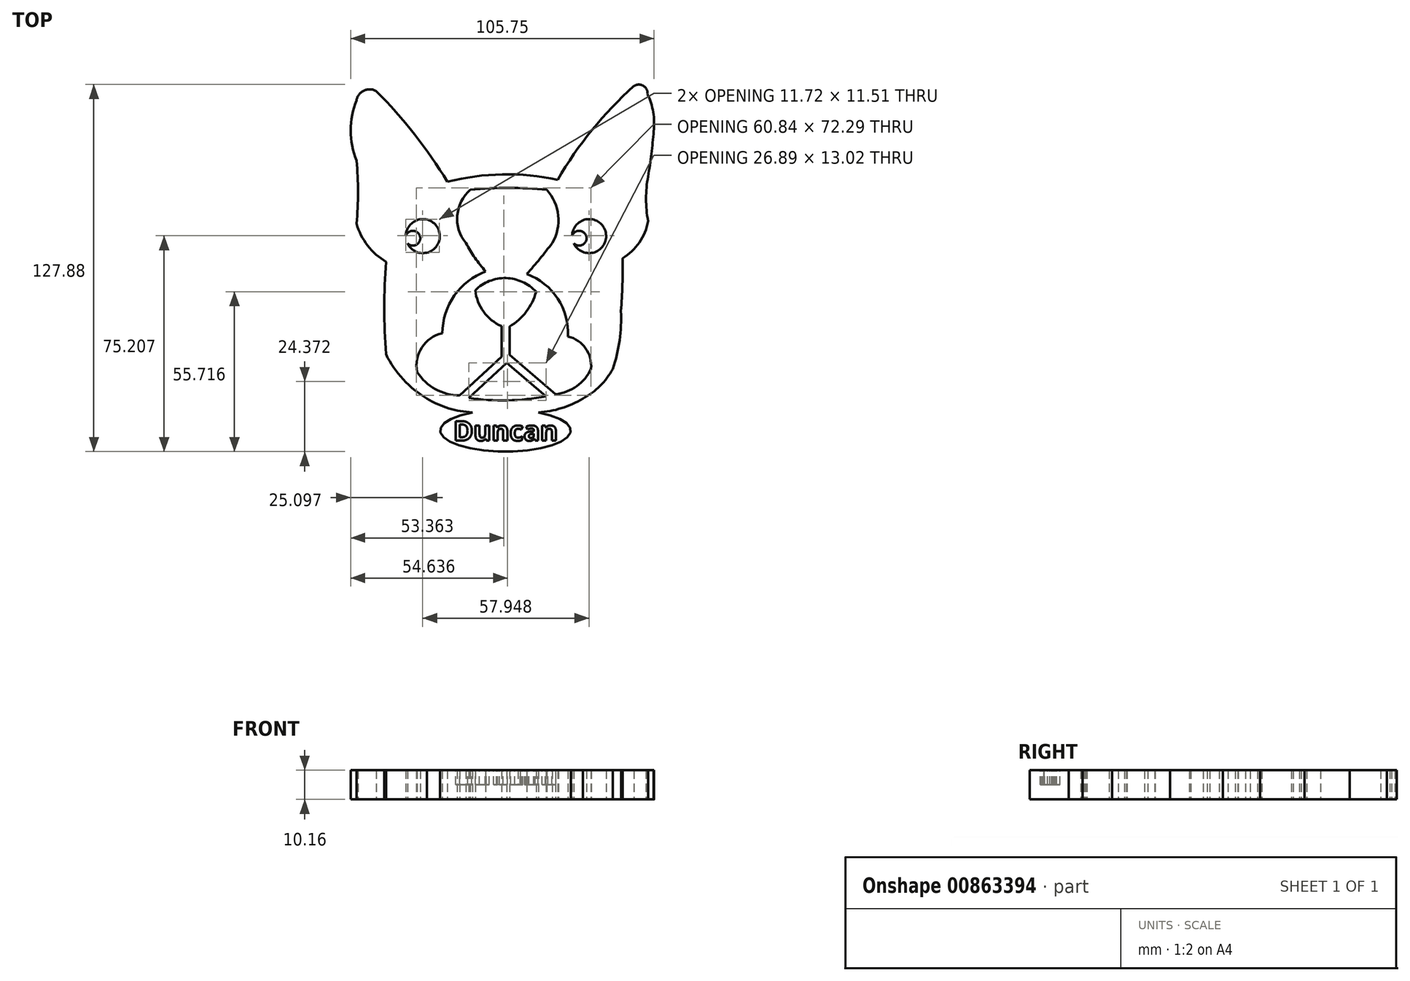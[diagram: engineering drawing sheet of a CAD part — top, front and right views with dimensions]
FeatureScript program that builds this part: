
annotation { "Feature Type Name" : "Feature", "Feature Type Description" : "" }
export const myFeature = defineFeature(function(context is Context, id is Id, definition is map)
    precondition{}
    {
        {
            var Q0;
            Q0=qCreatedBy(makeId("Top.planeOp"),FACE);
            var sketch = newSketch(context, id + "F0", { "sketchPlane" : qUnion([Q0])});
            skPoint(sketch, "E0", {"position": v(0, 0) * mm});
            skArc(sketch, "E1", {"start": v(19.56, 24.33) * mm, "mid": v(0.31, 26.2) * mm, "end": v(-18.85, 23.63) * mm});
            skArc(sketch, "E2", {"start": v(-18.85, 23.63) * mm, "mid": v(-30.3, 40.16) * mm, "end": v(-43.63, 55.21) * mm});
            skArc(sketch, "E3", {"start": v(-50.53, 9.03) * mm, "mid": v(-46.65, 1.42) * mm, "end": v(-40.27, -4.25) * mm});
            skArc(sketch, "E4", {"start": v(-50.53, 9.03) * mm, "mid": v(-50, 20) * mm, "end": v(-50.53, 30.98) * mm});
            skArc(sketch, "E5", {"start": v(-50.53, 52.04) * mm, "mid": v(-52.59, 41.5) * mm, "end": v(-50.53, 30.98) * mm});
            skArc(sketch, "E6", {"start": v(-43.63, 55.21) * mm, "mid": v(-47.9, 55.41) * mm, "end": v(-50.53, 52.04) * mm});
            skArc(sketch, "E7", {"start": v(46.1, 57) * mm, "mid": v(31.57, 41.69) * mm, "end": v(19.56, 24.33) * mm});
            skArc(sketch, "E8", {"start": v(42.14, -3) * mm, "mid": v(48.03, 2.47) * mm, "end": v(51.07, 9.91) * mm});
            skArc(sketch, "E9", {"start": v(51.07, 25.49) * mm, "mid": v(50.36, 17.7) * mm, "end": v(51.07, 9.91) * mm});
            skArc(sketch, "E10", {"start": v(51.07, 25.49) * mm, "mid": v(52.23, 33.34) * mm, "end": v(53.01, 41.24) * mm});
            skArc(sketch, "E11", {"start": v(50.89, 54.16) * mm, "mid": v(49.39, 57.08) * mm, "end": v(46.1, 57) * mm});
            skArc(sketch, "E12", {"start": v(53.01, 41.24) * mm, "mid": v(52.85, 47.85) * mm, "end": v(50.89, 54.16) * mm});
            skArc(sketch, "E13", {"start": v(-40.27, -4.25) * mm, "mid": v(-40.85, -20.36) * mm, "end": v(-40.27, -36.46) * mm});
            skArc(sketch, "E14", {"start": v(-40.27, -36.46) * mm, "mid": v(-34.27, -45.21) * mm, "end": v(-26.01, -51.87) * mm});
            skArc(sketch, "E15", {"start": v(-26.01, -51.87) * mm, "mid": v(-17.36, -55.6) * mm, "end": v(-8, -56.73) * mm});
            skArc(sketch, "E16", {"start": v(-8, -56.73) * mm, "mid": v(2.03, -57.3) * mm, "end": v(12.06, -56.73) * mm});
            skArc(sketch, "E17", {"start": v(12.06, -56.73) * mm, "mid": v(20.5, -55.35) * mm, "end": v(28.33, -51.87) * mm});
            skArc(sketch, "E18", {"start": v(28.33, -51.87) * mm, "mid": v(34.3, -47.5) * mm, "end": v(38.78, -41.6) * mm});
            skArc(sketch, "E19", {"start": v(38.78, -41.6) * mm, "mid": v(41.13, -31.64) * mm, "end": v(41.6, -21.42) * mm});
            skArc(sketch, "E20", {"start": v(41.6, -21.42) * mm, "mid": v(42.1, -12.22) * mm, "end": v(42.14, -3) * mm});
            skArc(sketch, "E21", {"start": v(-10.84, 20.83) * mm, "mid": v(-15.43, 11.9) * mm, "end": v(-12.41, 2.3) * mm});
            skArc(sketch, "E22", {"start": v(-12.41, 2.3) * mm, "mid": v(-9.27, -2.87) * mm, "end": v(-5.51, -7.61) * mm});
            skArc(sketch, "E23", {"start": v(15.73, 20.83) * mm, "mid": v(2.45, 21.5) * mm, "end": v(-10.84, 20.83) * mm});
            skArc(sketch, "E24", {"start": v(17.68, 2.3) * mm, "mid": v(19.73, 11.89) * mm, "end": v(15.73, 20.83) * mm});
            skArc(sketch, "E25", {"start": v(8.83, -8.5) * mm, "mid": v(13.36, -3.19) * mm, "end": v(17.68, 2.3) * mm});
            skArc(sketch, "E26", {"start": v(23.16, -30.27) * mm, "mid": v(19.53, -17.05) * mm, "end": v(8.83, -8.5) * mm});
            skArc(sketch, "E27", {"start": v(-5.51, -7.61) * mm, "mid": v(-16.44, -16) * mm, "end": v(-20.64, -29.14) * mm});
            skArc(sketch, "E28", {"start": v(31.16, -41.54) * mm, "mid": v(29.3, -34.39) * mm, "end": v(23.16, -30.27) * mm});
            skArc(sketch, "E29", {"start": v(12.06, -14.7) * mm, "mid": v(1.56, -9.93) * mm, "end": v(-9.17, -14.15) * mm});
            skArc(sketch, "E30", {"start": v(2.8, -26.81) * mm, "mid": v(8.59, -21.64) * mm, "end": v(12.06, -14.7) * mm});
            skArc(sketch, "E31", {"start": v(-9.17, -14.15) * mm, "mid": v(-6.25, -21.63) * mm, "end": v(0, -26.68) * mm});
            skLineSegment(sketch, "E32", {"start": v(2.8, -26.81) * mm, "end": v(2.8, -36.68) * mm});
            skLineSegment(sketch, "E33", {"start": v(2.8, -36.68) * mm, "end": v(18.87, -50.34) * mm});
            skLineSegment(sketch, "E34", {"start": v(-11.4, -51.66) * mm, "end": v(1.79, -39.49) * mm});
            skLineSegment(sketch, "E35", {"start": v(1.79, -39.49) * mm, "end": v(15.49, -51.13) * mm});
            skLineSegment(sketch, "E36", {"start": v(0, -26.68) * mm, "end": v(0, -37.34) * mm});
            skLineSegment(sketch, "E37", {"start": v(0, -37.34) * mm, "end": v(-14.58, -50.8) * mm});
            skArc(sketch, "E38.trimOffspring", {"start": v(-11.4, -51.66) * mm, "mid": v(2.07, -52.5) * mm, "end": v(15.49, -51.13) * mm});
            skArc(sketch, "E39", {"start": v(-29.42, -42.65) * mm, "mid": v(-23.03, -48.6) * mm, "end": v(-14.58, -50.8) * mm});
            skArc(sketch, "E40", {"start": v(-20.64, -29.14) * mm, "mid": v(-27.78, -34.11) * mm, "end": v(-29.42, -42.65) * mm});
            skArc(sketch, "E41", {"start": v(18.87, -50.34) * mm, "mid": v(26.2, -47.59) * mm, "end": v(31.16, -41.54) * mm});
            skArc(sketch, "E42", {"start": v(-32.8, 2.18) * mm, "mid": v(-21.64, 5.92) * mm, "end": v(-33.35, 4.84) * mm});
            skArc(sketch, "E43", {"start": v(-32.8, 2.18) * mm, "mid": v(-28.38, 4.5) * mm, "end": v(-33.35, 4.84) * mm});
            skArc(sketch, "E44", {"start": v(25.16, 2.18) * mm, "mid": v(36.31, 5.92) * mm, "end": v(24.6, 4.84) * mm});
            skArc(sketch, "E45", {"start": v(25.16, 2.18) * mm, "mid": v(29.56, 4.5) * mm, "end": v(24.6, 4.84) * mm});
            skSolve(sketch);
        }
        {
            var Q0;
            Q0 = qSketchRegion(id + "F0", true);
            extrude(context, id + "F1", {"entities" : qUnion([Q0]), "depth" : 10.16 * mm, "offsetDistance" : 25.4 * mm});
        }
        {
            var Q0;
            Q0=qCreatedBy(makeId("Top.planeOp"),FACE);
            var sketch = newSketch(context, id + "F2", { "sketchPlane" : qUnion([Q0])});
            skEllipse(sketch, "E46", {"center": v(1.36, -63.03) * mm, "majorRadius": 22.75 * mm, "minorRadius": 7.34 * mm, "majorAxis": v(1, 0)});
            skSolve(sketch);
        }
        {
            var Q0;
            Q0 = qSketchRegion(id + "F2", true);
            extrude(context, id + "F3", {"entities" : qUnion([Q0]), "operationType" : NewBodyOperationType.ADD, "depth" : 10.16 * mm, "offsetDistance" : 25.4 * mm});
        }
        {
            var Q0;
            Q0=makeQuery(id+"F3.boolean.opBoolean","MERGE",FACE,{"derivedFrom":[makeQuery(id+"F1.opExtrude","CAP_FACE",FACE,{"disambiguationData":[OSD([sQuery(id+"F0.wireOp",EDGE,"E1"),sQuery(id+"F0.wireOp",EDGE,"E2"),sQuery(id+"F0.wireOp",EDGE,"E3"),sQuery(id+"F0.wireOp",EDGE,"E4"),sQuery(id+"F0.wireOp",EDGE,"E5"),sQuery(id+"F0.wireOp",EDGE,"E6"),sQuery(id+"F0.wireOp",EDGE,"E7"),sQuery(id+"F0.wireOp",EDGE,"E8"),sQuery(id+"F0.wireOp",EDGE,"E9"),sQuery(id+"F0.wireOp",EDGE,"E10"),sQuery(id+"F0.wireOp",EDGE,"E11"),sQuery(id+"F0.wireOp",EDGE,"E12"),sQuery(id+"F0.wireOp",EDGE,"E13"),sQuery(id+"F0.wireOp",EDGE,"E14"),sQuery(id+"F0.wireOp",EDGE,"E15"),sQuery(id+"F0.wireOp",EDGE,"E16"),sQuery(id+"F0.wireOp",EDGE,"E17"),sQuery(id+"F0.wireOp",EDGE,"E18"),sQuery(id+"F0.wireOp",EDGE,"E19"),sQuery(id+"F0.wireOp",EDGE,"E20"),sQuery(id+"F0.wireOp",EDGE,"E21"),sQuery(id+"F0.wireOp",EDGE,"E22"),sQuery(id+"F0.wireOp",EDGE,"E23"),sQuery(id+"F0.wireOp",EDGE,"E24"),sQuery(id+"F0.wireOp",EDGE,"E25"),sQuery(id+"F0.wireOp",EDGE,"E26"),sQuery(id+"F0.wireOp",EDGE,"E27"),sQuery(id+"F0.wireOp",EDGE,"E28"),sQuery(id+"F0.wireOp",EDGE,"E29"),sQuery(id+"F0.wireOp",EDGE,"E30"),sQuery(id+"F0.wireOp",EDGE,"E31"),sQuery(id+"F0.wireOp",EDGE,"E32"),sQuery(id+"F0.wireOp",EDGE,"E33"),sQuery(id+"F0.wireOp",EDGE,"E34"),sQuery(id+"F0.wireOp",EDGE,"E35"),sQuery(id+"F0.wireOp",EDGE,"E36"),sQuery(id+"F0.wireOp",EDGE,"E37"),sQuery(id+"F0.wireOp",EDGE,"E38.trimOffspring"),sQuery(id+"F0.wireOp",EDGE,"E39"),sQuery(id+"F0.wireOp",EDGE,"E40"),sQuery(id+"F0.wireOp",EDGE,"E41"),sQuery(id+"F0.wireOp",EDGE,"E42"),sQuery(id+"F0.wireOp",EDGE,"E43"),sQuery(id+"F0.wireOp",EDGE,"E44"),sQuery(id+"F0.wireOp",EDGE,"E45")])],"isStart":false}),makeQuery(id+"F3.opExtrude","CAP_FACE",FACE,{"disambiguationData":[OSD([sQuery(id+"F2.wireOp",EDGE,"E46")])],"isStart":false})]});
            var sketch = newSketch(context, id + "F4", { "sketchPlane" : qUnion([Q0])});
            skText(sketch, "E47", { "text": "Duncan", "fontName": "OpenSans-Bold.ttf"});
            skPoint(sketch, "E48", {"position": v(1.36, -70.37) * mm});
            const initialGuessF4  = {"E47": [-0.01684, -0.06656, 1, 0, 0.00686]};
            skSetInitialGuess(sketch, initialGuessF4);
            skSolve(sketch);
        }
        {
            var Q0;
            Q0 = qSketchRegion(id + "F4", true);
            extrude(context, id + "F5", {"entities" : qUnion([Q0]), "operationType" : NewBodyOperationType.REMOVE, "oppositeDirection" : true, "depth" : 5.08 * mm, "offsetDistance" : 25.4 * mm});
        }
    });
